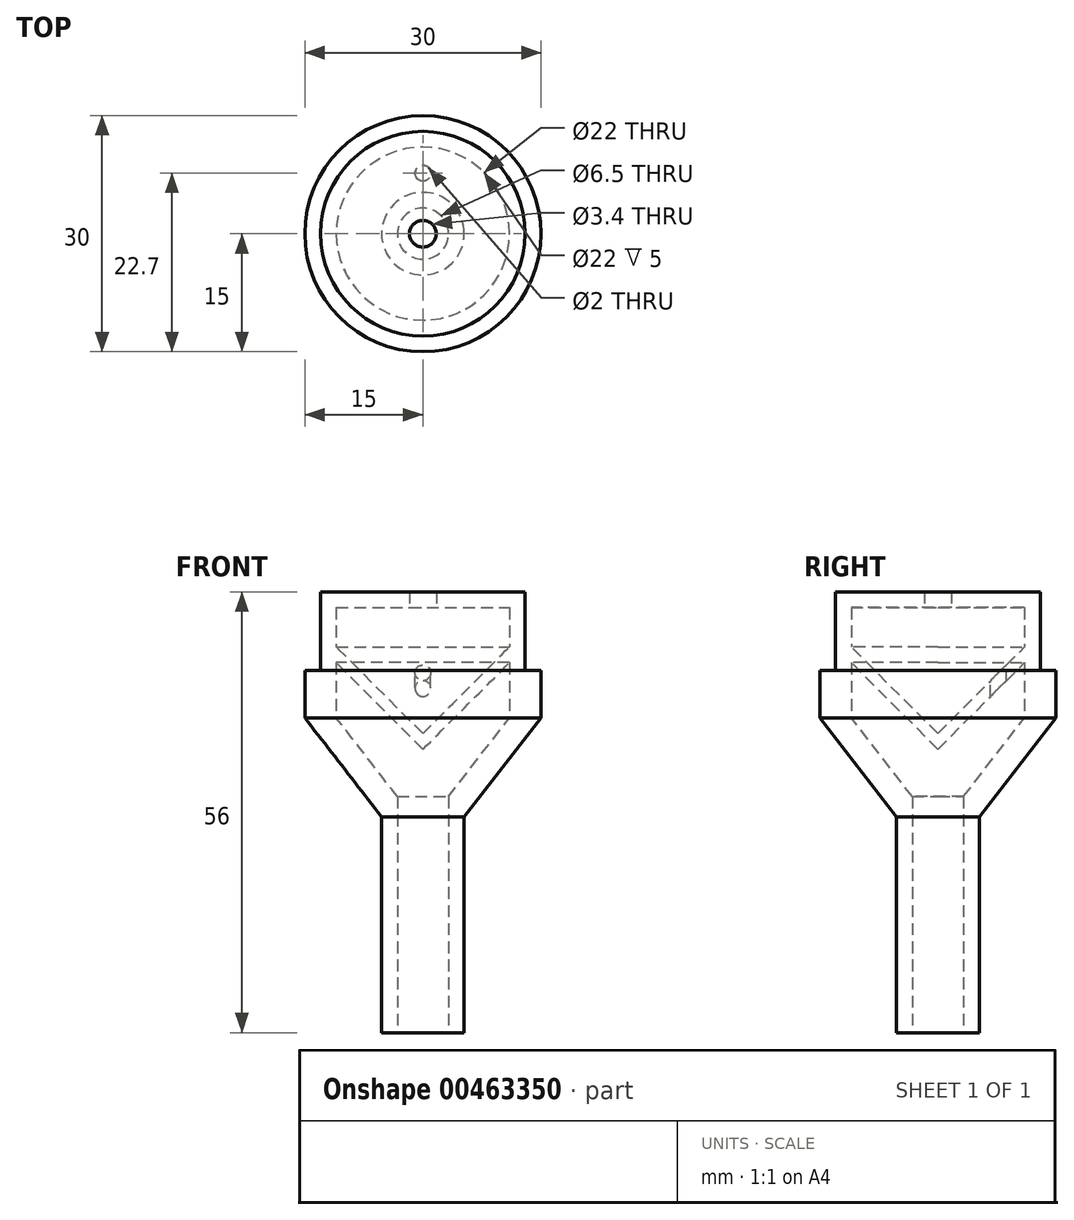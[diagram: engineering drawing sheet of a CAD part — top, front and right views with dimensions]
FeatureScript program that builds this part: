
annotation { "Feature Type Name" : "Feature", "Feature Type Description" : "" }
export const myFeature = defineFeature(function(context is Context, id is Id, definition is map)
    precondition{}
    {
        {
            var Q0;
            Q0=qCreatedBy(makeId("Front.planeOp"),FACE);
            var sketch = newSketch(context, id + "F0", { "sketchPlane" : qUnion([Q0])});
            skLineSegment(sketch, "E0", {"start": v(0, 0) * mm, "end": v(0, 30) * mm, "construction": true});
            skLineSegment(sketch, "E1", {"start": v(5.25, 27.42) * mm, "end": v(5.25, 0) * mm});
            skLineSegment(sketch, "E2", {"start": v(3.25, 30) * mm, "end": v(3.25, 0) * mm});
            skLineSegment(sketch, "E3", {"start": v(3.25, 0) * mm, "end": v(5.25, 0) * mm});
            skLineSegment(sketch, "E4", {"start": v(5.25, 27.42) * mm, "end": v(15, 40) * mm});
            skLineSegment(sketch, "E5", {"start": v(15, 40) * mm, "end": v(15, 46) * mm});
            skLineSegment(sketch, "E6", {"start": v(5.25, 27.42) * mm, "end": v(3.25, 30) * mm, "construction": true});
            skLineSegment(sketch, "E7.trimOffspring", {"start": v(11, 54) * mm, "end": v(11, 49) * mm});
            skLineSegment(sketch, "E8", {"start": v(11, 54) * mm, "end": v(1.7, 54) * mm});
            skLineSegment(sketch, "E9", {"start": v(1.7, 54) * mm, "end": v(1.7, 56) * mm});
            skLineSegment(sketch, "E10", {"start": v(1.7, 56) * mm, "end": v(13, 56) * mm});
            skLineSegment(sketch, "E11", {"start": v(3.25, 30) * mm, "end": v(11, 40) * mm});
            skLineSegment(sketch, "E12", {"start": v(11, 49) * mm, "end": v(0, 38) * mm});
            skLineSegment(sketch, "E13", {"start": v(0, 38) * mm, "end": v(0, 36) * mm});
            skLineSegment(sketch, "E14", {"start": v(0, 36) * mm, "end": v(11, 47) * mm});
            skLineSegment(sketch, "E15.trimOffspring", {"start": v(11, 47) * mm, "end": v(11, 40) * mm});
            skLineSegment(sketch, "E16", {"start": v(11, 47) * mm, "end": v(11, 49) * mm, "construction": true});
            skLineSegment(sketch, "E17", {"start": v(15, 46) * mm, "end": v(13, 46) * mm});
            skLineSegment(sketch, "E18", {"start": v(13, 46) * mm, "end": v(13, 56) * mm});
            skLineSegment(sketch, "E19", {"start": v(15, 40) * mm, "end": v(11, 40) * mm, "construction": true});
            skLineSegment(sketch, "E20", {"start": v(13, 46) * mm, "end": v(11, 46) * mm, "construction": true});
            skSolve(sketch);
        }
        {
            var Q0;
            Q0=makeQuery(id+"F0.imprint","IMPRINT",FACE,{"disambiguationData":[TD([[makeQuery(id+"F0.imprint","IMPRINT",EDGE,{"derivedFrom":sQuery(id+"F0.wireOp",EDGE,"E1")}),-1.0]])]});
            var Q1;
            Q1=sQuery(id+"F0.wireOp",EDGE,"E0");
            revolve(context, id + "F1", {"entities" : qUnion([Q0]), "axis" : qUnion([Q1]), "revolveType" : RevolveType.FULL});
        }
        {
            var Q0;
            Q0=makeQuery(id+"F1.opRevolve","SWEPT_FACE",FACE,{"disambiguationData":[OSD([sQuery(id+"F0.wireOp",EDGE,"E10")])]});
            cPlane(context, id + "F2", {"entities" : qUnion([Q0]), "cplaneType" : CPlaneType.OFFSET, "offset" : 5 * mm, "oppositeDirection" : true, "width" : 150 * mm, "height" : 150 * mm});
        }
        {
            var Q0;
            Q0=qCreatedBy(id+"F2.planeOp",FACE);
            var sketch = newSketch(context, id + "F3", { "sketchPlane" : qUnion([Q0])});
            skPoint(sketch, "E21", {"position": v(0, 7.7) * mm});
            skSolve(sketch);
        }
        {
            var Q0;
            Q0=sQuery(id+"F3.wireOp",VERTEX,"E21");
            var Q1;
            Q1=makeQuery(id+"F1.opRevolve","SWEPT_BODY",BODY,{"disambiguationData":[OSD([sQuery(id+"F0.wireOp",EDGE,"E1"),sQuery(id+"F0.wireOp",EDGE,"E2"),sQuery(id+"F0.wireOp",EDGE,"E3"),sQuery(id+"F0.wireOp",EDGE,"E4"),sQuery(id+"F0.wireOp",EDGE,"E5"),sQuery(id+"F0.wireOp",EDGE,"AV9xxQl0-xnfg-gOsV-8vPH-NjQAOvubr44c"),sQuery(id+"F0.wireOp",EDGE,"3hiZnHQe-UQ1D-VN4d-As7d-uXD5AKtEw2LT"),sQuery(id+"F0.wireOp",EDGE,"Qnl0nGyi-H9qm-ebai-0Zov-qSfluJZPxokn"),sQuery(id+"F0.wireOp",EDGE,"54R6ySEB-fWiY-6u6A-Jmir-oRQqmOqZ26i4"),sQuery(id+"F0.wireOp",EDGE,"11397222-02e9-46d7-a949-95fa1dcd65c4.trimOffspring"),sQuery(id+"F0.wireOp",EDGE,"E7.trimOffspring"),sQuery(id+"F0.wireOp",EDGE,"E8"),sQuery(id+"F0.wireOp",EDGE,"E9"),sQuery(id+"F0.wireOp",EDGE,"E10")])]});
            hole(context, id + "F4", {"style" : HoleStyle.SIMPLE, "endStyle" : HoleEndStyle.BLIND, "holeDiameter" : 2 * mm, "holeDepth" : 3 * mm, "isTappedThrough" : true, "tappedDepth" : 12 * mm, "tapClearance" : 3, "locations" : qUnion([Q0]), "scope" : qUnion([Q1])});
        }
    });
